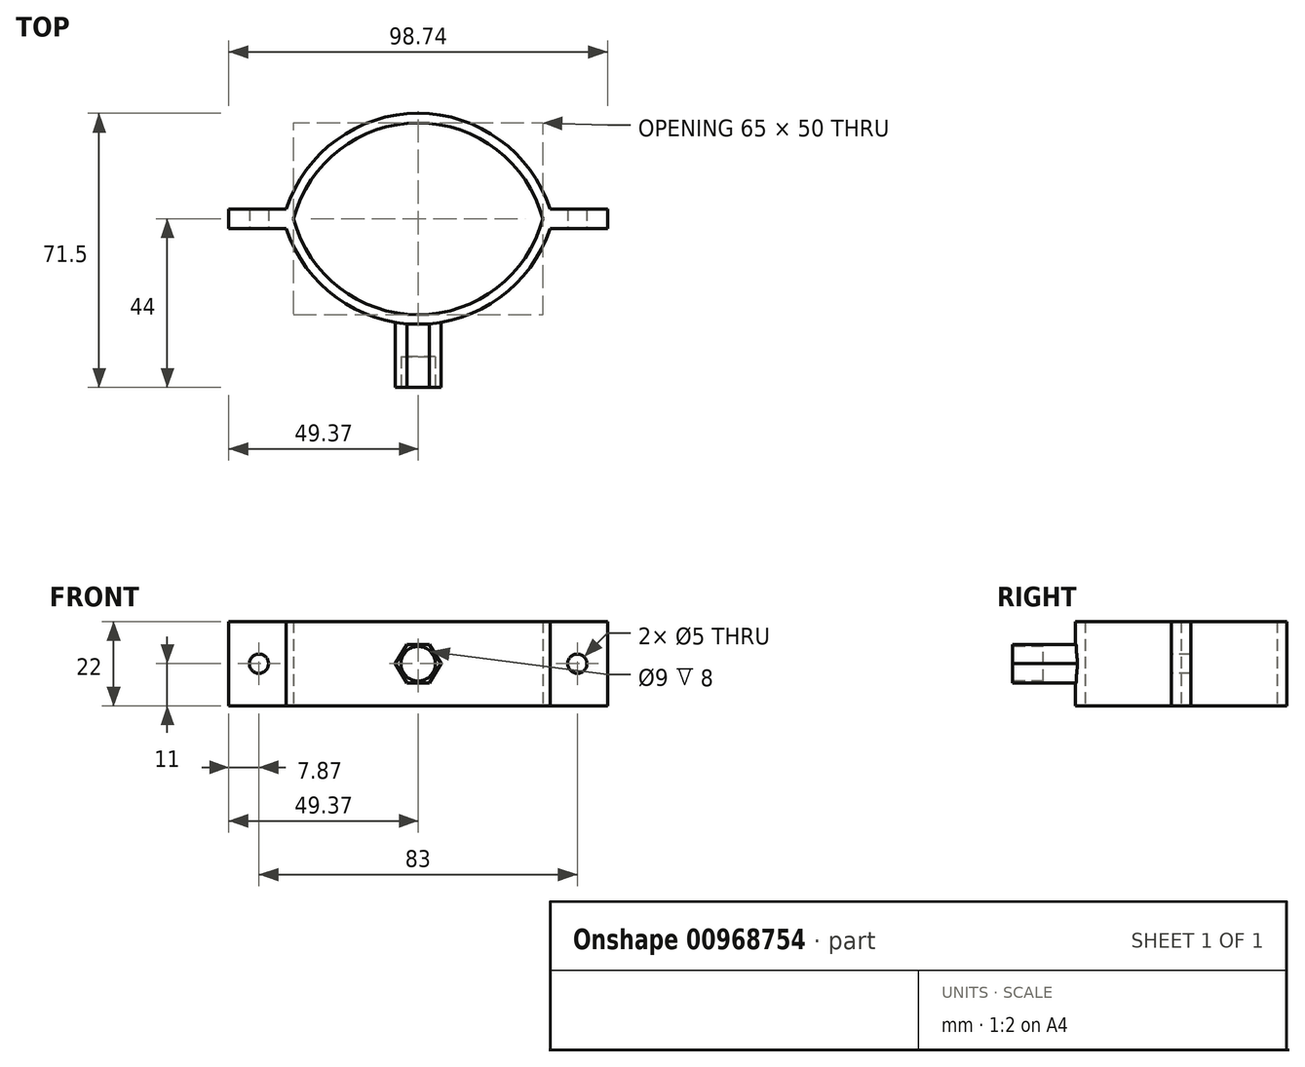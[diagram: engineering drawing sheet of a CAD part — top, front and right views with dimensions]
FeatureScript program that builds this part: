
annotation { "Feature Type Name" : "Feature", "Feature Type Description" : "" }
export const myFeature = defineFeature(function(context is Context, id is Id, definition is map)
    precondition{}
    {
        {
            var Q0;
            Q0=qCreatedBy(makeId("Top.planeOp"),FACE);
            var sketch = newSketch(context, id + "F0", { "sketchPlane" : qUnion([Q0])});
            skArc(sketch, "E0", {"start": v(32.5, 0) * mm, "mid": v(0, 25) * mm, "end": v(-32.5, 0) * mm});
            skLineSegment(sketch, "E1", {"start": v(-32.5, 0) * mm, "end": v(-49.37, 0) * mm});
            skLineSegment(sketch, "E2", {"start": v(-49.37, 0) * mm, "end": v(-49.37, 2.5) * mm});
            skLineSegment(sketch, "E3", {"start": v(-49.37, 2.5) * mm, "end": v(-34.37, 2.5) * mm});
            skLineSegment(sketch, "E4", {"start": v(32.5, 0) * mm, "end": v(49.37, 0) * mm});
            skLineSegment(sketch, "E5", {"start": v(49.37, 0) * mm, "end": v(49.37, 2.5) * mm});
            skLineSegment(sketch, "E6", {"start": v(49.37, 2.5) * mm, "end": v(34.37, 2.5) * mm});
            skArc(sketch, "E7", {"start": v(34.37, 2.5) * mm, "mid": v(0, 27.5) * mm, "end": v(-34.37, 2.5) * mm});
            skLineSegment(sketch, "E8.MirrorCS", {"start": v(49.37, 0) * mm, "end": v(49.37, -2.5) * mm});
            skLineSegment(sketch, "E9.MirrorCS", {"start": v(-49.37, 0) * mm, "end": v(-49.37, -2.5) * mm});
            skLineSegment(sketch, "E10.MirrorCS", {"start": v(-49.37, -2.5) * mm, "end": v(-34.37, -2.5) * mm});
            skLineSegment(sketch, "E11.MirrorCS", {"start": v(49.37, -2.5) * mm, "end": v(34.37, -2.5) * mm});
            skArc(sketch, "E12.MirrorCS", {"start": v(34.37, -2.5) * mm, "mid": v(0, -27.5) * mm, "end": v(-34.37, -2.5) * mm});
            skArc(sketch, "E13.MirrorCS", {"start": v(32.5, 0) * mm, "mid": v(0, -25) * mm, "end": v(-32.5, 0) * mm});
            skSolve(sketch);
        }
        {
            var Q0;
            Q0=qSketchRegion(id+"F0",true);
            extrude(context, id + "F1", {"entities" : qUnion([Q0]), "depth" : 22 * mm, "offsetDistance" : 25 * mm});
        }
        {
            var Q0;
            Q0=qCreatedBy(makeId("Front.planeOp"),FACE);
            cPlane(context, id + "F2", {"entities" : qUnion([Q0]), "cplaneType" : CPlaneType.OFFSET, "offset" : 25 * mm, "width" : 150 * mm, "height" : 150 * mm});
        }
        {
            var Q0;
            Q0=qCreatedBy(id+"F2.planeOp",FACE);
            var sketch = newSketch(context, id + "F3", { "sketchPlane" : qUnion([Q0])});
            skLineSegment(sketch, "E14", {"start": v(2.93, 16) * mm, "end": v(-2.93, 16) * mm});
            skLineSegment(sketch, "E15", {"start": v(-2.93, 16) * mm, "end": v(-6, 11) * mm});
            skLineSegment(sketch, "E16", {"start": v(-6, 11) * mm, "end": v(-2.93, 6) * mm});
            skLineSegment(sketch, "E17", {"start": v(-2.93, 6) * mm, "end": v(2.93, 6) * mm});
            skLineSegment(sketch, "E18", {"start": v(2.93, 6) * mm, "end": v(6, 11) * mm});
            skLineSegment(sketch, "E19", {"start": v(2.93, 16) * mm, "end": v(6, 11) * mm});
            skSolve(sketch);
        }
        {
            var Q0;
            Q0=qSketchRegion(id+"F3",true);
            extrude(context, id + "F4", {"entities" : qUnion([Q0]), "operationType" : NewBodyOperationType.ADD, "depth" : 19 * mm, "offsetDistance" : 25 * mm});
        }
        {
            var Q0;
            Q0=makeQuery(id+"F1.opExtrude","SWEPT_FACE",FACE,{"disambiguationData":[OSD([sQuery(id+"F0.wireOp",EDGE,"E11.MirrorCS")])]});
            var sketch = newSketch(context, id + "F5", { "sketchPlane" : qUnion([Q0])});
            skCircle(sketch, "E20", {"center": v(41.5, 11) * mm, "radius": 2.5 * mm});
            skCircle(sketch, "E21", {"center": v(-41.5, 11) * mm, "radius": 2.5 * mm});
            skSolve(sketch);
        }
        {
            var Q0;
            Q0=qSketchRegion(id+"F5",true);
            extrude(context, id + "F6", {"entities" : qUnion([Q0]), "operationType" : NewBodyOperationType.REMOVE, "endBound" : BoundingType.UP_TO_NEXT, "oppositeDirection" : true, "depth" : 25 * mm, "offsetDistance" : 25 * mm});
        }
        {
            var Q0;
            Q0=makeQuery(id+"F4.opExtrude","CAP_FACE",FACE,{"disambiguationData":[OSD([sQuery(id+"F3.wireOp",EDGE,"E14"),sQuery(id+"F3.wireOp",EDGE,"E15"),sQuery(id+"F3.wireOp",EDGE,"E16"),sQuery(id+"F3.wireOp",EDGE,"E17"),sQuery(id+"F3.wireOp",EDGE,"E18"),sQuery(id+"F3.wireOp",EDGE,"E19")])],"isStart":false});
            var sketch = newSketch(context, id + "F7", { "sketchPlane" : qUnion([Q0])});
            skCircle(sketch, "E22", {"center": v(0, 11) * mm, "radius": 4.5 * mm});
            skSolve(sketch);
        }
        {
            var Q0;
            Q0=qSketchRegion(id+"F7",true);
            extrude(context, id + "F8", {"entities" : qUnion([Q0]), "operationType" : NewBodyOperationType.REMOVE, "oppositeDirection" : true, "depth" : 8 * mm, "offsetDistance" : 25 * mm});
        }
    });
